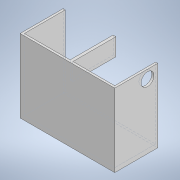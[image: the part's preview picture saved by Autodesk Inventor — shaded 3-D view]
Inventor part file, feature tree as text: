
AUTODESK INVENTOR PART (.ipt)
format: ipt  version: 2020 (Build 240168000, 168)  size: 127,488 bytes
history: native  units: mm
features: extrude x5, sketch x5
ambient origin geometry x8: Origin, YZ Plane, XZ Plane, XY Plane, X Axis, Y Axis, Z Axis, Center Point
bodies: Solid1 (feature_tree)
feature tree (10):
  extrude  "Extrusion1"  Depth=170.0mm
  extrude  "Extrusion2"  Depth=210.0mm
  extrude  "Extrusion3"  Depth=95.0mm TaperAngle=0.0deg
  extrude  "Extrusion4"  Depth=5.0mm
  extrude  "Extrusion5"  Depth=100.0mm TaperAngle=0.0deg
  sketch  "Sketch1"  dims[d0=220.0mm d1=170.0mm]
  sketch  "Sketch2"  dims[d2=100.0mm d3=0.0mm d4=210.0mm]
  sketch  "Sketch3"  dims[d5=240.0mm d6=95.0mm d7=0.0mm]
  sketch  "Sketch4"  dims[d8=5.0mm d9=30.0mm]
  sketch  "Sketch5"  dims[d10=20.0mm d11=45.0mm d12=0.0mm d13=5.0mm d14=10.0mm d15=0.0mm d16=100.0mm d17=0.0mm]
